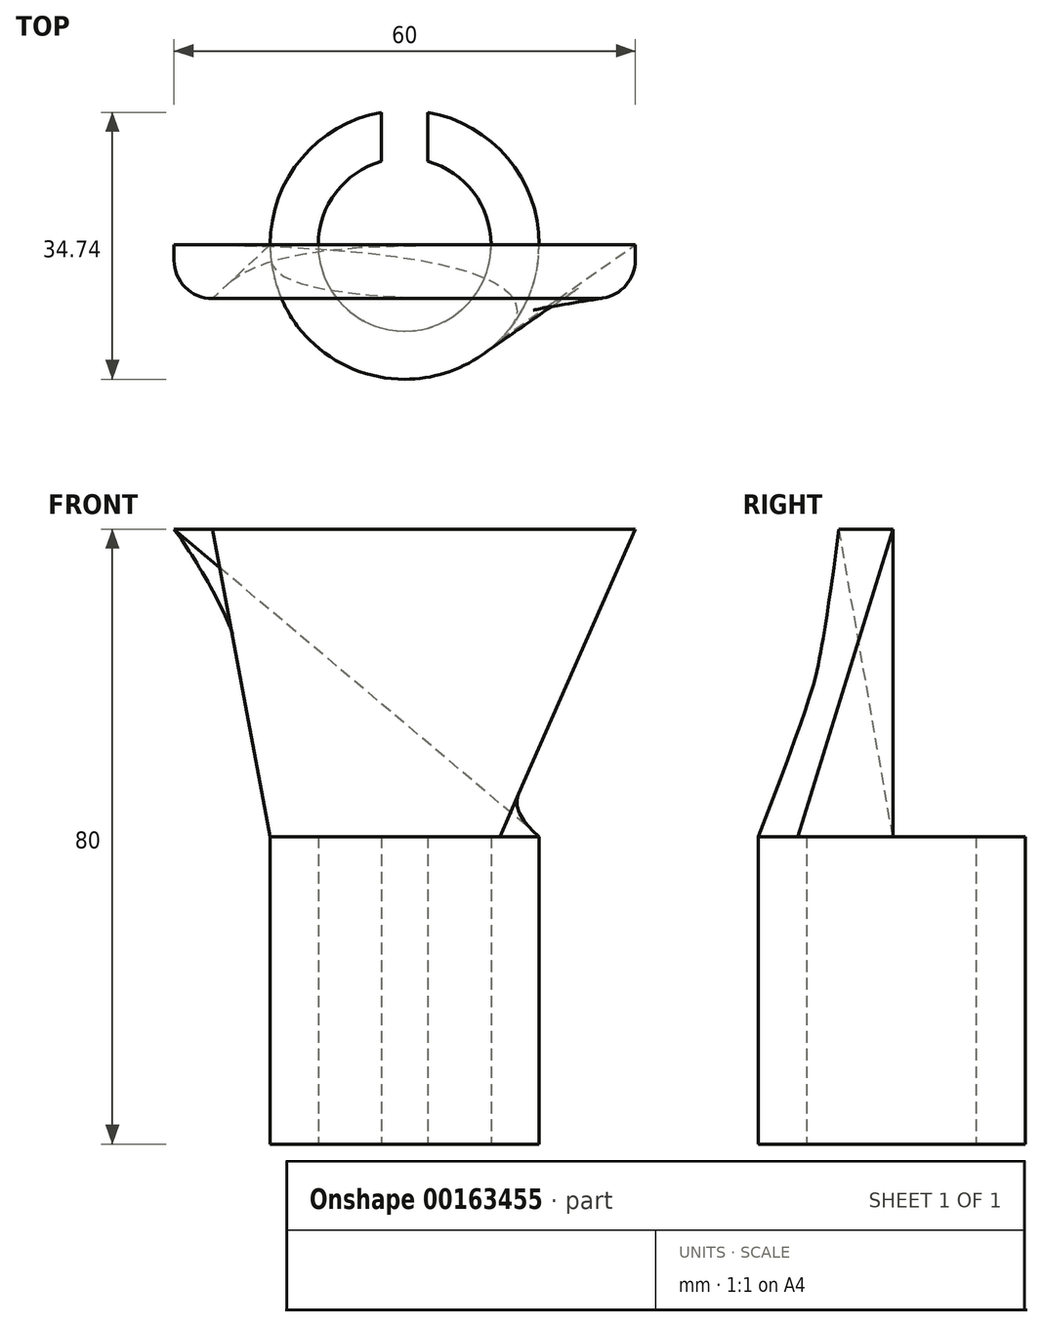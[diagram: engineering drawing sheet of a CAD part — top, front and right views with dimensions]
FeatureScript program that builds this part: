
annotation { "Feature Type Name" : "Feature", "Feature Type Description" : "" }
export const myFeature = defineFeature(function(context is Context, id is Id, definition is map)
    precondition{}
    {
        {
            var Q0;
            Q0=qCreatedBy(makeId("Top.planeOp"),FACE);
            var sketch = newSketch(context, id + "F0", { "sketchPlane" : qUnion([Q0])});
            skArc(sketch, "E0", {"start": v(-3, 17.24) * mm, "mid": v(0, -17.5) * mm, "end": v(3, 17.24) * mm});
            skArc(sketch, "E1", {"start": v(-3, 10.84) * mm, "mid": v(0, -11.25) * mm, "end": v(3, 10.84) * mm});
            skLineSegment(sketch, "E2.left", {"start": v(3, 17.24) * mm, "end": v(3, 10.84) * mm});
            skLineSegment(sketch, "E2.right", {"start": v(-3, 17.24) * mm, "end": v(-3, 10.84) * mm});
            skSolve(sketch);
        }
        {
            var Q0;
            Q0 = qSketchRegion(id + "F0", true);
            extrude(context, id + "F1", {"entities" : qUnion([Q0]), "depth" : 40 * mm});
        }
        {
            var Q0;
            Q0=makeQuery(id+"F1.opExtrude","CAP_FACE",FACE,{"disambiguationData":[OSD([sQuery(id+"F0.wireOp",EDGE,"E0"),sQuery(id+"F0.wireOp",EDGE,"E1"),sQuery(id+"F0.wireOp",EDGE,"E2.left"),sQuery(id+"F0.wireOp",EDGE,"E2.right")])],"isStart":false});
            var sketch = newSketch(context, id + "F2", { "sketchPlane" : qUnion([Q0])});
            skLineSegment(sketch, "E3", {"start": v(-17.5, 0) * mm, "end": v(17.5, 0) * mm});
            skArc(sketch, "E4.0", {"start": v(-17.5, 0) * mm, "mid": v(0, -17.5) * mm, "end": v(17.5, 0) * mm});
            skPoint(sketch, "E5.orphan", {"position": v(3, 17.24) * mm});
            skPoint(sketch, "E6.orphan", {"position": v(-3, 17.24) * mm});
            skSolve(sketch);
        }
        {
            var Q0;
            {var subQ0=sQuery(id+"F2.wireOp",EDGE,"E4.0");Q0=makeQuery(id+"F2.imprint","IMPRINT",FACE,{"disambiguationData":[TD([[makeQuery(id+"F2.imprint","IMPRINT",EDGE,{"derivedFrom":subQ0}),1.0]])]});}
            cPlane(context, id + "F3", {"entities" : qUnion([Q0]), "cplaneType" : CPlaneType.OFFSET, "offset" : 40 * mm, "width" : 150 * mm, "height" : 150 * mm});
        }
        {
            var Q0;
            Q0=qCreatedBy(id+"F3.planeOp",FACE);
            var sketch = newSketch(context, id + "F4", { "sketchPlane" : qUnion([Q0])});
            skLineSegment(sketch, "E7", {"start": v(-30, 0) * mm, "end": v(30, 0) * mm});
            skPoint(sketch, "E8.visualSharp", {"position": v(30, 0) * mm});
            skPoint(sketch, "E9.visualSharp", {"position": v(-30, 0) * mm});
            skLineSegment(sketch, "E10", {"start": v(-30, 0) * mm, "end": v(-30, -2) * mm});
            skLineSegment(sketch, "E11", {"start": v(-25, -7) * mm, "end": v(25, -7) * mm});
            skLineSegment(sketch, "E12", {"start": v(30, -2) * mm, "end": v(30, 0) * mm});
            skPoint(sketch, "E13.visualSharp", {"position": v(-30, -7) * mm});
            skArc(sketch, "E13.filletArc", {"start": v(-30, -2) * mm, "mid": v(-28.54, -5.54) * mm, "end": v(-25, -7) * mm});
            skPoint(sketch, "E14.visualSharp", {"position": v(30, -7) * mm});
            skArc(sketch, "E14.filletArc", {"start": v(25, -7) * mm, "mid": v(28.54, -5.54) * mm, "end": v(30, -2) * mm});
            skSolve(sketch);
        }
        {
            var Q1;
            Q1 = qSketchRegion(id + "F2", true);
            var Q2;
            Q2 = qSketchRegion(id + "F4", true);
            loft(context, id + "F5", {"operationType" : NewBodyOperationType.ADD, "sheetProfilesArray" : [{ "sheetProfileEntities" : qUnion([Q1]) }, { "sheetProfileEntities" : qUnion([Q2]) }]});
        }
    });
